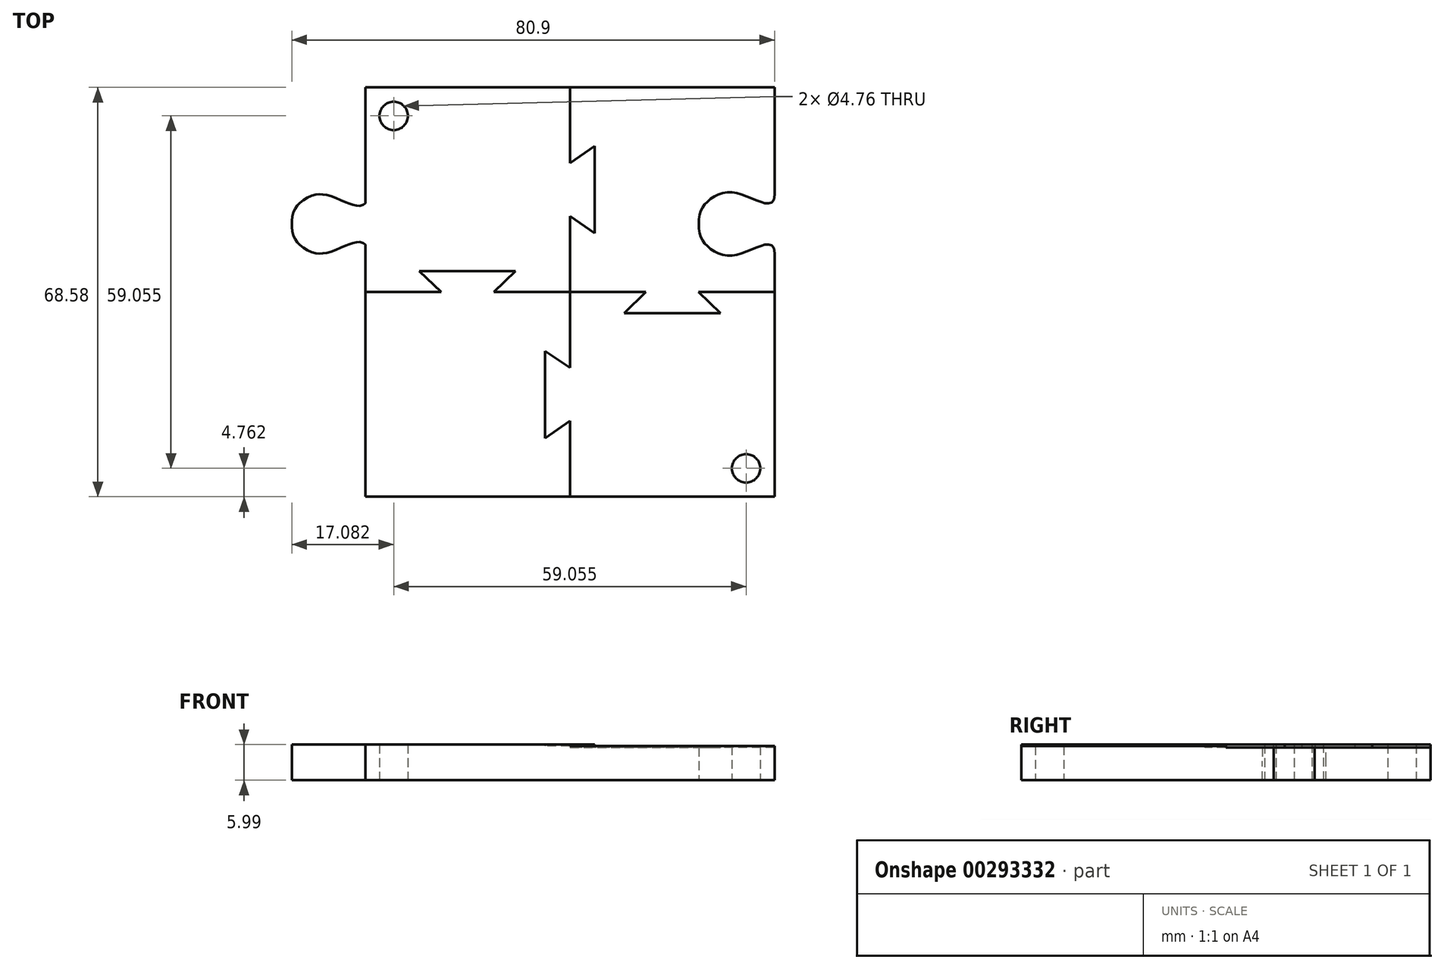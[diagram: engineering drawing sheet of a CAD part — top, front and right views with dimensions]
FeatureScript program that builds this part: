
annotation { "Feature Type Name" : "Feature", "Feature Type Description" : "" }
export const myFeature = defineFeature(function(context is Context, id is Id, definition is map)
    precondition{}
    {
        {
            var Q0;
            Q0=qCreatedBy(makeId("Top.planeOp"),FACE);
            var sketch = newSketch(context, id + "F0", { "sketchPlane" : qUnion([Q0])});
            skLineSegment(sketch, "E0.bottom", {"start": v(34.3, 34.3) * mm, "end": v(-34.3, 34.3) * mm});
            skLineSegment(sketch, "E0.top", {"start": v(34.3, -34.3) * mm, "end": v(-34.3, -34.3) * mm});
            skLineSegment(sketch, "E0.left", {"start": v(34.3, 34.3) * mm, "end": v(34.3, -34.3) * mm});
            skLineSegment(sketch, "E0.right", {"start": v(-34.3, 34.3) * mm, "end": v(-34.3, -34.3) * mm});
            skPoint(sketch, "E0.middle", {"position": v(0, 0) * mm});
            skCircle(sketch, "E1", {"center": v(-29.53, 29.53) * mm, "radius": 2.38 * mm});
            skCircle(sketch, "E2.MirrorC", {"center": v(29.53, -29.53) * mm, "radius": 2.38 * mm});
            skSolve(sketch);
        }
        {
            var Q0;
            Q0=qSketchRegion(id+"F0",true);
            extrude(context, id + "F1", {"entities" : qUnion([Q0]), "depth" : 3.17 * mm});
        }
        {
            var Q0;
            Q0=qCreatedBy(makeId("Top.planeOp"),FACE);
            var sketch = newSketch(context, id + "F2", { "sketchPlane" : qUnion([Q0])});
            skPoint(sketch, "E3", {"position": v(-34.3, 16.33) * mm});
            skPoint(sketch, "E4", {"position": v(-36.2, 14.99) * mm});
            skPoint(sketch, "E5", {"position": v(-41.66, 16.76) * mm});
            skPoint(sketch, "E6", {"position": v(-45.72, 14.99) * mm});
            skPoint(sketch, "E7", {"position": v(-47, 11.43) * mm});
            skFitSpline(sketch, "E8", {"points": [v(-34.3, 16.33) * mm, v(-36.2, 14.99) * mm, v(-41.66, 16.76) * mm, v(-45.72, 14.99) * mm, v(-47, 11.43) * mm], "startDerivative": vector(0, -24.54) * mm, "endDerivative": vector(0, -20.15) * mm});
            skLineSegment(sketch, "E9", {"start": v(-47, 11.43) * mm, "end": v(-29.95, 11.43) * mm, "construction": true});
            skFitSpline(sketch, "E10.MirrorCS", {"points": [v(-34.3, 6.53) * mm, v(-36.2, 7.87) * mm, v(-41.66, 6.1) * mm, v(-45.72, 7.87) * mm, v(-47, 11.43) * mm], "startDerivative": vector(0, 24.54) * mm, "endDerivative": vector(0, 20.15) * mm});
            skLineSegment(sketch, "E11", {"start": v(-34.3, 16.33) * mm, "end": v(-34.3, 6.53) * mm, "construction": true});
            skFitSpline(sketch, "E12.MirrorCS", {"points": [v(-34.3, 16.33) * mm, v(-32.39, 14.99) * mm, v(-26.92, 16.76) * mm, v(-22.86, 14.99) * mm, v(-21.59, 11.43) * mm], "startDerivative": vector(0, -24.54) * mm, "endDerivative": vector(0, -20.15) * mm});
            skFitSpline(sketch, "E13.MirrorCS", {"points": [v(-34.3, 6.53) * mm, v(-32.39, 7.87) * mm, v(-26.92, 6.1) * mm, v(-22.86, 7.87) * mm, v(-21.59, 11.43) * mm], "startDerivative": vector(0, 24.54) * mm, "endDerivative": vector(0, 20.15) * mm});
            skFitSpline(sketch, "E14.0", {"points": [v(-33.9, 6.53) * mm, v(-33.9, 6.8) * mm, v(-33.96, 7.3) * mm, v(-34.16, 7.77) * mm, v(-34.42, 8.07) * mm, v(-34.73, 8.28) * mm, v(-35.16, 8.4) * mm, v(-35.7, 8.38) * mm, v(-36.22, 8.27) * mm, v(-36.76, 8.1) * mm, v(-37.5, 7.83) * mm, v(-38.44, 7.42) * mm, v(-39.6, 6.94) * mm, v(-40.54, 6.64) * mm, v(-41.28, 6.5) * mm, v(-41.8, 6.46) * mm, v(-42.32, 6.5) * mm, v(-43, 6.62) * mm, v(-43.8, 6.91) * mm, v(-44.68, 7.44) * mm, v(-45.29, 7.96) * mm, v(-45.69, 8.4) * mm, v(-46.02, 8.85) * mm, v(-46.33, 9.45) * mm, v(-46.56, 10.3) * mm, v(-46.6, 11.03) * mm, v(-46.6, 11.43) * mm]});
            skFitSpline(sketch, "E14.1", {"points": [v(-33.9, 16.33) * mm, v(-33.9, 16.05) * mm, v(-33.96, 15.56) * mm, v(-34.16, 15.09) * mm, v(-34.42, 14.8) * mm, v(-34.73, 14.58) * mm, v(-35.16, 14.46) * mm, v(-35.7, 14.48) * mm, v(-36.22, 14.6) * mm, v(-36.76, 14.76) * mm, v(-37.5, 15.03) * mm, v(-38.44, 15.44) * mm, v(-39.6, 15.92) * mm, v(-40.54, 16.22) * mm, v(-41.28, 16.36) * mm, v(-41.8, 16.4) * mm, v(-42.32, 16.37) * mm, v(-43, 16.24) * mm, v(-43.8, 15.95) * mm, v(-44.68, 15.42) * mm, v(-45.29, 14.9) * mm, v(-45.69, 14.46) * mm, v(-46.02, 14.01) * mm, v(-46.33, 13.41) * mm, v(-46.56, 12.55) * mm, v(-46.6, 11.83) * mm, v(-46.6, 11.43) * mm]});
            skLineSegment(sketch, "E15", {"start": v(-34.3, 16.33) * mm, "end": v(-34.3, 6.53) * mm});
            skLineSegment(sketch, "E16", {"start": v(-34.3, 7.92) * mm, "end": v(-34.3, 14.94) * mm});
            skFitSpline(sketch, "E17.MirrorCS", {"points": [v(34.3, 16.33) * mm, v(32.39, 14.99) * mm, v(26.92, 16.76) * mm, v(22.86, 14.99) * mm, v(21.59, 11.43) * mm], "startDerivative": vector(0, -24.54) * mm, "endDerivative": vector(0, -20.15) * mm});
            skFitSpline(sketch, "E18.MirrorCS", {"points": [v(34.3, 6.53) * mm, v(32.39, 7.87) * mm, v(26.92, 6.1) * mm, v(22.86, 7.87) * mm, v(21.59, 11.43) * mm], "startDerivative": vector(0, 24.54) * mm, "endDerivative": vector(0, 20.15) * mm});
            skLineSegment(sketch, "E19", {"start": v(34.3, 16.33) * mm, "end": v(39.12, 16.33) * mm});
            skLineSegment(sketch, "E20", {"start": v(39.12, 16.33) * mm, "end": v(39.12, 6.53) * mm});
            skLineSegment(sketch, "E21", {"start": v(39.12, 6.53) * mm, "end": v(34.3, 6.53) * mm});
            skSolve(sketch);
        }
        {
            var Q0;
            Q0=makeQuery(id+"F2.imprint","IMPRINT",FACE,{"disambiguationData":[TD([[makeQuery(id+"F2.imprint","IMPRINT",EDGE,{"derivedFrom":sQuery(id+"F2.wireOp",EDGE,"E14.0")}),-1.0]])]});
            var Q1;
            Q1=makeQuery(id+"F1.opExtrude","CAP_FACE",FACE,{"disambiguationData":[OSD([sQuery(id+"F0.wireOp",EDGE,"E0.bottom"),sQuery(id+"F0.wireOp",EDGE,"E0.top"),sQuery(id+"F0.wireOp",EDGE,"E0.left"),sQuery(id+"F0.wireOp",EDGE,"E0.right"),sQuery(id+"F0.wireOp",EDGE,"E1"),sQuery(id+"F0.wireOp",EDGE,"e1648c08-8adf-473f-9b64-c467cf328ef90.MirrorC"),sQuery(id+"F0.wireOp",EDGE,"1cdcda55-2210-49d8-b5f0-9198a802923b0.MirrorC"),sQuery(id+"F0.wireOp",EDGE,"E2.MirrorC")])],"isStart":false});
            extrude(context, id + "F3", {"entities" : qUnion([Q0]), "operationType" : NewBodyOperationType.ADD, "endBound" : BoundingType.UP_TO_SURFACE, "endBoundEntityFace" : qUnion([Q1]), "depth" : 25.4 * mm});
        }
        {
            var Q0;
            Q0=qCreatedBy(makeId("Right.planeOp"),FACE);
            var sketch = newSketch(context, id + "F4", { "sketchPlane" : qUnion([Q0])});
            skLineSegment(sketch, "E22", {"start": v(0, -65.87) * mm, "end": v(0, 47.63) * mm});
            skSolve(sketch);
        }
        {
            var Q0;
            Q0=makeQuery(id+"F2.imprint","IMPRINT",FACE,{"disambiguationData":[TD([[makeQuery(id+"F2.imprint","IMPRINT",EDGE,{"derivedFrom":sQuery(id+"F2.wireOp",EDGE,"E17.MirrorCS")}),1.0]])]});
            extrude(context, id + "F5", {"entities" : qUnion([Q0]), "operationType" : NewBodyOperationType.REMOVE, "endBound" : BoundingType.THROUGH_ALL, "depth" : 25.4 * mm});
        }
        {
            var Q0;
            {var subQ0=sQuery(id+"F0.wireOp",EDGE,"E2.MirrorC");var subQ1=sQuery(id+"F0.wireOp",EDGE,"E1");var subQ2=sQuery(id+"F0.wireOp",EDGE,"E0.right");var subQ3=sQuery(id+"F0.wireOp",EDGE,"E0.left");var subQ4=sQuery(id+"F0.wireOp",EDGE,"E0.top");var subQ5=sQuery(id+"F0.wireOp",EDGE,"E0.bottom");Q0=makeQuery(id+"FDfX84p6046V9zH_1.3.F3.boolean.opBoolean","MERGE",FACE,{"derivedFrom":[makeQuery(id+"FDfX84p6046V9zH_1.2.F3.boolean.opBoolean","MERGE",FACE,{"derivedFrom":[makeQuery(id+"FDfX84p6046V9zH_1.1.F3.boolean.opBoolean","MERGE",FACE,{"derivedFrom":[makeQuery(id+"F3.boolean.opBoolean","MERGE",FACE,{"derivedFrom":[makeQuery(id+"F1.opExtrude","CAP_FACE",FACE,{"disambiguationData":[OSD([subQ5,subQ4,subQ3,subQ2,subQ1,subQ0])],"isStart":false}),makeQuery(id+"F3.opExtrude","CAP_FACE",FACE,{"disambiguationData":[OSD([subQ5,subQ4,subQ3,subQ2,subQ1,subQ0])],"isStart":false})]}),makeQuery(id+"FDfX84p6046V9zH_1.1.F3.opExtrude","CAP_FACE",FACE,{"disambiguationData":[OSD([subQ5,subQ4,subQ3,subQ2,subQ1,subQ0])],"isStart":false})]}),makeQuery(id+"FDfX84p6046V9zH_1.2.F3.opExtrude","CAP_FACE",FACE,{"disambiguationData":[OSD([subQ5,subQ4,subQ3,subQ2,subQ1,subQ0])],"isStart":false})]}),makeQuery(id+"FDfX84p6046V9zH_1.3.F3.opExtrude","CAP_FACE",FACE,{"disambiguationData":[OSD([subQ5,subQ4,subQ3,subQ2,subQ1,subQ0])],"isStart":false})]});}
            var sketch = newSketch(context, id + "F6", { "sketchPlane" : qUnion([Q0])});
            skLineSegment(sketch, "E23", {"start": v(-34.3, 0) * mm, "end": v(-21.58, 0) * mm});
            skLineSegment(sketch, "E24", {"start": v(-21.58, 0) * mm, "end": v(-25.25, 3.52) * mm});
            skLineSegment(sketch, "E25", {"start": v(0, 0) * mm, "end": v(-12.73, 0) * mm});
            skLineSegment(sketch, "E26", {"start": v(-12.73, 0) * mm, "end": v(-9.11, 3.52) * mm});
            skLineSegment(sketch, "E27", {"start": v(-9.11, 3.52) * mm, "end": v(-25.25, 3.52) * mm});
            skLineSegment(sketch, "E28.MirrorCS", {"start": v(34.3, 0) * mm, "end": v(21.58, 0) * mm});
            skLineSegment(sketch, "E29.MirrorCS", {"start": v(0, 0) * mm, "end": v(12.73, 0) * mm});
            skLineSegment(sketch, "E30.MirrorCS", {"start": v(9.11, -3.52) * mm, "end": v(25.25, -3.52) * mm});
            skLineSegment(sketch, "E31.MirrorCS", {"start": v(12.73, 0) * mm, "end": v(9.11, -3.52) * mm});
            skLineSegment(sketch, "E32.MirrorCS", {"start": v(21.58, 0) * mm, "end": v(25.25, -3.52) * mm});
            skPoint(sketch, "E33.MirrorCS.start.orphan", {"position": v(-12.73, 0) * mm});
            skPoint(sketch, "E34.MirrorCS.start.orphan", {"position": v(-21.58, 0) * mm});
            skLineSegment(sketch, "E35", {"start": v(0, 34.3) * mm, "end": v(0, 21.6) * mm});
            skLineSegment(sketch, "E36", {"start": v(0, 21.6) * mm, "end": v(4.16, 24.51) * mm});
            skLineSegment(sketch, "E37", {"start": v(0, 0) * mm, "end": v(0, 12.7) * mm});
            skLineSegment(sketch, "E38", {"start": v(0, 12.7) * mm, "end": v(4.16, 9.86) * mm});
            skLineSegment(sketch, "E39", {"start": v(4.16, 9.86) * mm, "end": v(4.16, 24.51) * mm});
            skLineSegment(sketch, "E40.MirrorCS", {"start": v(0, 0) * mm, "end": v(0, -12.7) * mm});
            skLineSegment(sketch, "E41.MirrorCS", {"start": v(0, -34.3) * mm, "end": v(0, -21.6) * mm});
            skLineSegment(sketch, "E42.MirrorCS", {"start": v(0, -12.7) * mm, "end": v(-4.16, -9.86) * mm});
            skLineSegment(sketch, "E43.MirrorCS", {"start": v(-4.16, -9.86) * mm, "end": v(-4.16, -24.51) * mm});
            skLineSegment(sketch, "E44.MirrorCS", {"start": v(0, -21.6) * mm, "end": v(-4.16, -24.51) * mm});
            skPoint(sketch, "E45.MirrorCS.start.orphan", {"position": v(0, -12.7) * mm});
            skPoint(sketch, "E46.MirrorCS.start.orphan", {"position": v(0, -21.6) * mm});
            skSolve(sketch);
        }
        {
            var Q0;
            {var subQ1=sQuery(id+"F6.wireOp",EDGE,"E28.MirrorCS");Q0=makeQuery(id+"F6.imprint","IMPRINT",FACE,{"disambiguationData":[TD([[makeQuery(id+"F6.imprint","IMPRINT",EDGE,{"derivedFrom":subQ1}),1.0]])]});}
            extrude(context, id + "F7", {"entities" : qUnion([Q0]), "operationType" : NewBodyOperationType.ADD, "depth" : 2.54 * mm});
        }
        {
            var Q0;
            {var subQ22=sQuery(id+"F6.wireOp",EDGE,"E23");Q0=makeQuery(id+"F6.imprint","IMPRINT",FACE,{"disambiguationData":[TD([[makeQuery(id+"F6.imprint","IMPRINT",EDGE,{"derivedFrom":subQ22}),-1.0]])]});}
            extrude(context, id + "F8", {"entities" : qUnion([Q0]), "operationType" : NewBodyOperationType.ADD, "depth" : 2.8 * mm});
        }
        {
            var Q0;
            {var subQ21=sQuery(id+"F6.wireOp",EDGE,"E23");Q0=makeQuery(id+"F6.imprint","IMPRINT",FACE,{"disambiguationData":[TD([[makeQuery(id+"F6.imprint","IMPRINT",EDGE,{"derivedFrom":subQ21}),1.0]])]});}
            extrude(context, id + "F9", {"entities" : qUnion([Q0]), "operationType" : NewBodyOperationType.ADD, "depth" : 2.82 * mm});
        }
        {
            var Q0;
            {var subQ0=sQuery(id+"F0.wireOp",EDGE,"E2.MirrorC");var subQ1=sQuery(id+"F0.wireOp",EDGE,"E1");var subQ2=sQuery(id+"F0.wireOp",EDGE,"E0.right");var subQ3=sQuery(id+"F0.wireOp",EDGE,"E0.left");var subQ4=sQuery(id+"F0.wireOp",EDGE,"E0.top");var subQ5=sQuery(id+"F0.wireOp",EDGE,"E0.bottom");Q0=makeQuery(id+"FDfX84p6046V9zH_1.3.F3.boolean.opBoolean","MERGE",FACE,{"derivedFrom":[makeQuery(id+"FDfX84p6046V9zH_1.2.F3.boolean.opBoolean","MERGE",FACE,{"derivedFrom":[makeQuery(id+"FDfX84p6046V9zH_1.1.F3.boolean.opBoolean","MERGE",FACE,{"derivedFrom":[makeQuery(id+"F3.boolean.opBoolean","MERGE",FACE,{"derivedFrom":[makeQuery(id+"F1.opExtrude","CAP_FACE",FACE,{"disambiguationData":[OSD([subQ5,subQ4,subQ3,subQ2,subQ1,subQ0])],"isStart":false}),makeQuery(id+"F3.opExtrude","CAP_FACE",FACE,{"disambiguationData":[OSD([subQ5,subQ4,subQ3,subQ2,subQ1,subQ0])],"isStart":false})]}),makeQuery(id+"FDfX84p6046V9zH_1.1.F3.opExtrude","CAP_FACE",FACE,{"disambiguationData":[OSD([subQ5,subQ4,subQ3,subQ2,subQ1,subQ0])],"isStart":false})]}),makeQuery(id+"FDfX84p6046V9zH_1.2.F3.opExtrude","CAP_FACE",FACE,{"disambiguationData":[OSD([subQ5,subQ4,subQ3,subQ2,subQ1,subQ0])],"isStart":false})]}),makeQuery(id+"FDfX84p6046V9zH_1.3.F3.opExtrude","CAP_FACE",FACE,{"disambiguationData":[OSD([subQ5,subQ4,subQ3,subQ2,subQ1,subQ0])],"isStart":false})]});}
            extrude(context, id + "F10", {"entities" : qUnion([Q0]), "operationType" : NewBodyOperationType.ADD, "depth" : 2.3 * mm});
        }
    });
